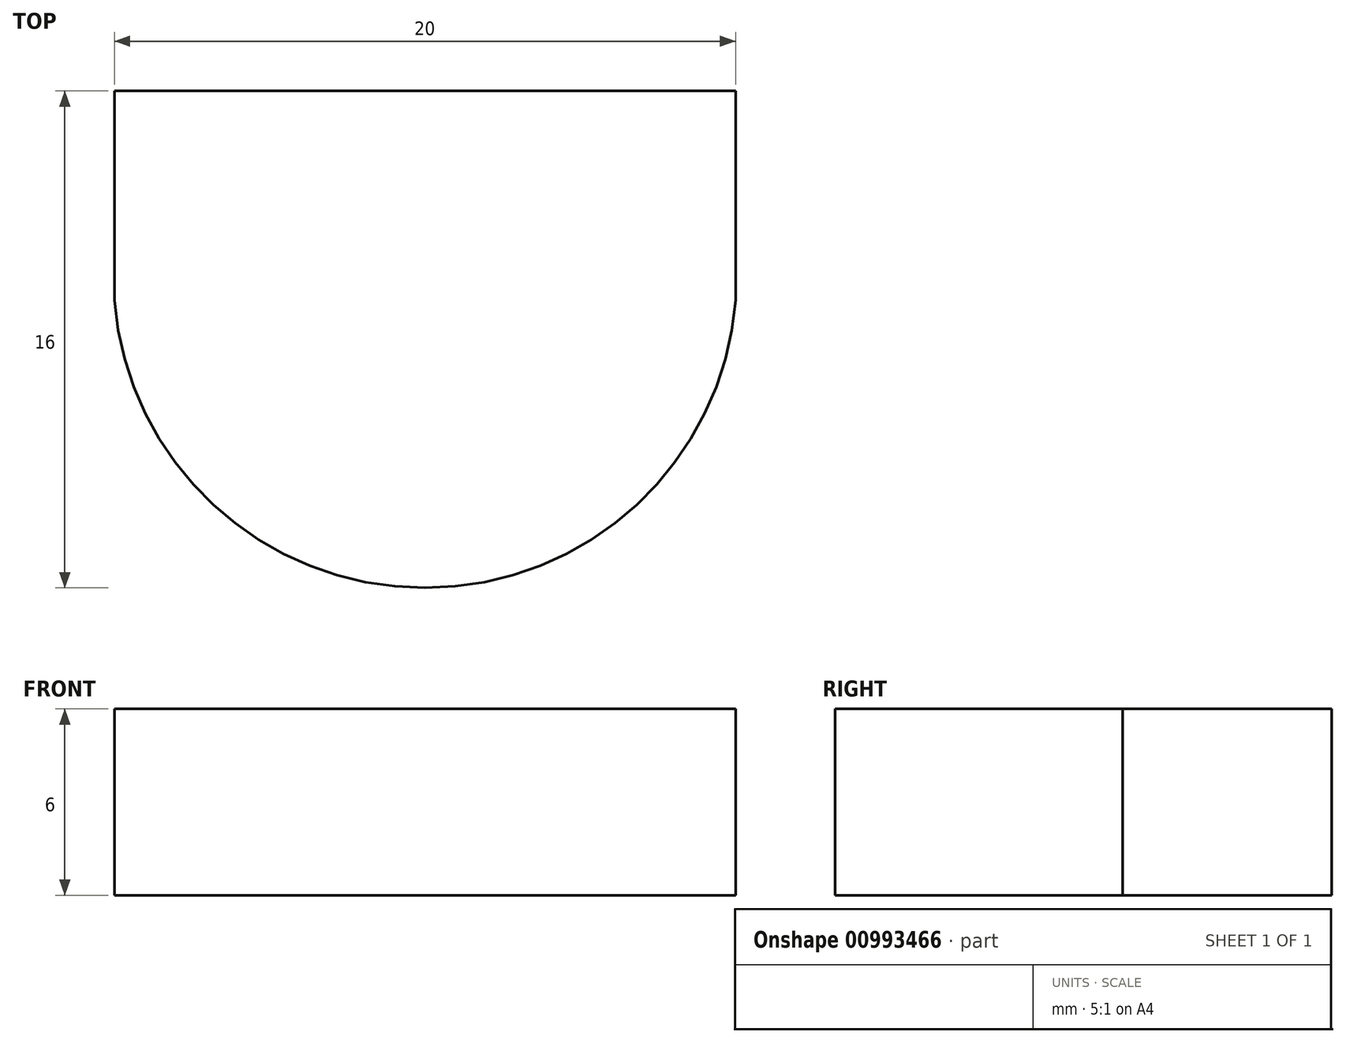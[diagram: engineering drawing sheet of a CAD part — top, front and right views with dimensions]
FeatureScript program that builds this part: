
annotation { "Feature Type Name" : "Feature", "Feature Type Description" : "" }
export const myFeature = defineFeature(function(context is Context, id is Id, definition is map)
    precondition{}
    {
        {
            var Q0;
            Q0=qCreatedBy(makeId("Top.planeOp"),FACE);
            var sketch = newSketch(context, id + "F0", { "sketchPlane" : qUnion([Q0])});
            skLineSegment(sketch, "E0.top", {"start": v(-10, -6.74) * mm, "end": v(10, -6.74) * mm});
            skPoint(sketch, "E0.middle", {"position": v(0, 0) * mm});
            skArc(sketch, "E1", {"start": v(-10, -6.74) * mm, "mid": v(0, -16) * mm, "end": v(10, -6.74) * mm});
            skLineSegment(sketch, "E2", {"start": v(-10, 0) * mm, "end": v(10, 0) * mm});
            skLineSegment(sketch, "E3.top", {"start": v(-6.69, 0) * mm, "end": v(0.9, 0) * mm});
            skLineSegment(sketch, "E4", {"start": v(-10, -6.74) * mm, "end": v(-10, 0) * mm});
            skLineSegment(sketch, "E5", {"start": v(10, -6.74) * mm, "end": v(10, 0) * mm});
            skSolve(sketch);
        }
        {
            var Q0;
            {var subQ5=makeQuery(id+"F0.imprint","IMPRINT",EDGE,{"derivedFrom":sQuery(id+"F0.wireOp",EDGE,"E0.top")});Q0=qUnion([makeQuery(id+"F0.imprint","IMPRINT",FACE,{"disambiguationData":[TD([[subQ5,-1.0]])]}),makeQuery(id+"F0.imprint","IMPRINT",FACE,{"disambiguationData":[TD([[subQ5,1.0]])]})]);}
            extrude(context, id + "F1", {"entities" : qUnion([Q0]), "depth" : 6 * mm, "offsetDistance" : 25 * mm});
        }
    });
